# Revit family: Strangregulierventil mit Messblende 4017 M
name_source: partatom
category: Rohrzubehör
units: mm (PartAtom-declared; Revit-internal decimal feet)

## family parameters
Arbeitsebenenbasiert = Nein
Beim Laden mit Abzugskörper schneiden = Nein
Bemaßung runder Anschluss = Durchmesser verwenden
Gemeinsam genutzt = Nein
Immer vertikal = Ja
OmniClass-Nummer = 23.65.55.14
OmniClass-Titel = Valves for Liquid Services
Teiletyp = Unterbricht

## types (2) — shared parameters
Anwendungsgebiet = Zum hydraulischen Abgleich in Heiz- oder Kühlanlagen, Einregulieren von Verteilleitungen, Strängen, Wärmetauschern,
Heiz- und Kühlregistern.
Ausführung = STRÖMAX 4017 M, Strangregulierventil mit Messblende für Differenzdruckmessung in Schrägsitzform, mit Messventilen
Gelbe Ausführung aus entzinkungsbeständigen Messing, Muffe x Muffe, Spindelabdichtung mit Dreifach-O-Ring, Voreinstellung durch Hubbegrenzung, digitale Anzeige der Voreinstellstufe im Handradfenster.
Gehäuse = entzinkungsbeständiges Messing
H02 = 13 mm
Hersteller = HERZ Armaturen Ges.m.b.H.
Max.Betriebsdruck = 2000000.0 Pa
Max.Betriebstemperatur = 130 °C
Max.Differenzdruck bei geschlossenen Sitz = 1000000.0 Pa
Medium = Heizwasserqualität entsprechend ÖNORM H 5195 bzw. VDI-Richtlinie 2035
R01 = 12 mm  [stored 0.0393701 ft]
R02 = 9.5 mm  [stored 0.031168 ft]
R03 = 21.5 mm
S03 = 60 mm  [stored 0.19685 ft]
SCRNCODE = 05;07;02
SCRNSEQ = ARM;ARM_TYP="STRV";2
SW01 = 60.00°
URL = www.herz-armaturen.at
W01 = 50.00°
zero-valued in all types: E00, SC_NennweiteBerechnet, Vorgabe-Ansicht

## per-type parameters (varying)
| type | Dämmung |
| ohne Dämmung | Nein |
| mit Dämmung | Ja |

note: [stored X ft] marks values corroborated as IEEE doubles in the binary element streams (Revit-internal decimal feet)
